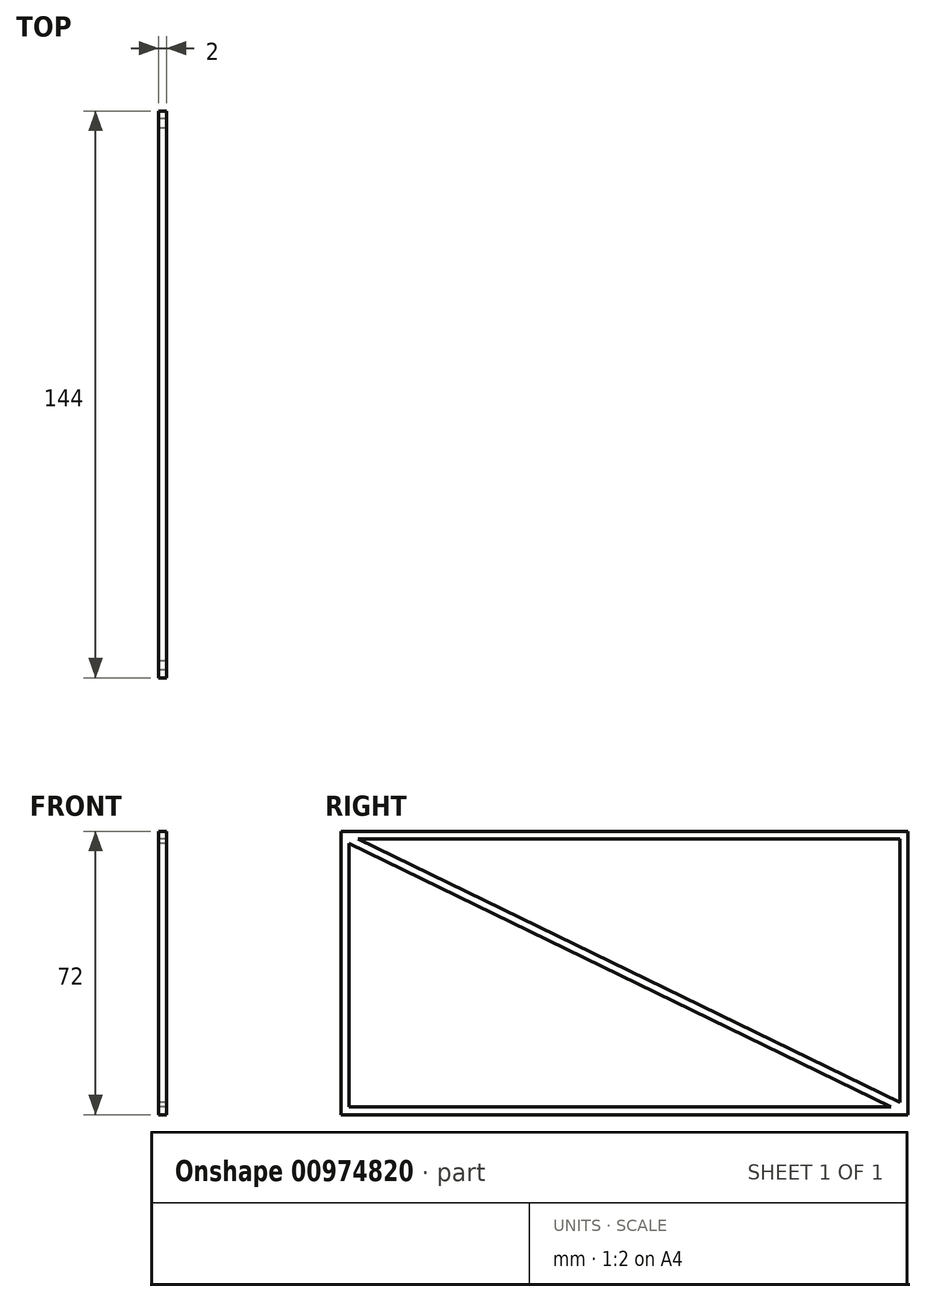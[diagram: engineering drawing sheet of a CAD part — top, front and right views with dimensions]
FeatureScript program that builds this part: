
annotation { "Feature Type Name" : "Feature", "Feature Type Description" : "" }
export const myFeature = defineFeature(function(context is Context, id is Id, definition is map)
    precondition{}
    {
        {
            var Q0;
            Q0=qCreatedBy(makeId("Right.planeOp"),FACE);
            var sketch = newSketch(context, id + "F0", { "sketchPlane" : qUnion([Q0])});
            skLineSegment(sketch, "E0.bottom", {"start": v(0, 0) * mm, "end": v(144, 0) * mm});
            skLineSegment(sketch, "E0.top", {"start": v(0, 72) * mm, "end": v(144, 72) * mm});
            skLineSegment(sketch, "E0.left", {"start": v(0, 0) * mm, "end": v(0, 72) * mm});
            skLineSegment(sketch, "E0.right", {"start": v(144, 0) * mm, "end": v(144, 72) * mm});
            skLineSegment(sketch, "E1", {"start": v(2, 2) * mm, "end": v(2, 68.89) * mm});
            skLineSegment(sketch, "E2", {"start": v(2, 68.89) * mm, "end": v(139.71, 2) * mm});
            skLineSegment(sketch, "E3", {"start": v(139.71, 2) * mm, "end": v(2, 2) * mm});
            skLineSegment(sketch, "E4", {"start": v(142, 70) * mm, "end": v(142, 3.11) * mm});
            skLineSegment(sketch, "E5", {"start": v(142, 3.11) * mm, "end": v(4.29, 70) * mm});
            skLineSegment(sketch, "E6", {"start": v(4.29, 70) * mm, "end": v(142, 70) * mm});
            skLineSegment(sketch, "E7.bottom", {"start": v(142, 70) * mm, "end": v(2, 70) * mm, "construction": true});
            skLineSegment(sketch, "E7.left", {"start": v(142, 70) * mm, "end": v(142, 2) * mm, "construction": true});
            skLineSegment(sketch, "E8", {"start": v(2, 70) * mm, "end": v(142, 2) * mm, "construction": true});
            skSolve(sketch);
        }
        {
            var Q0;
            Q0 = qSketchRegion(id + "F0", true);
            extrude(context, id + "F1", {"entities" : qUnion([Q0]), "depth" : 2 * mm, "offsetDistance" : 25 * mm});
        }
    });
